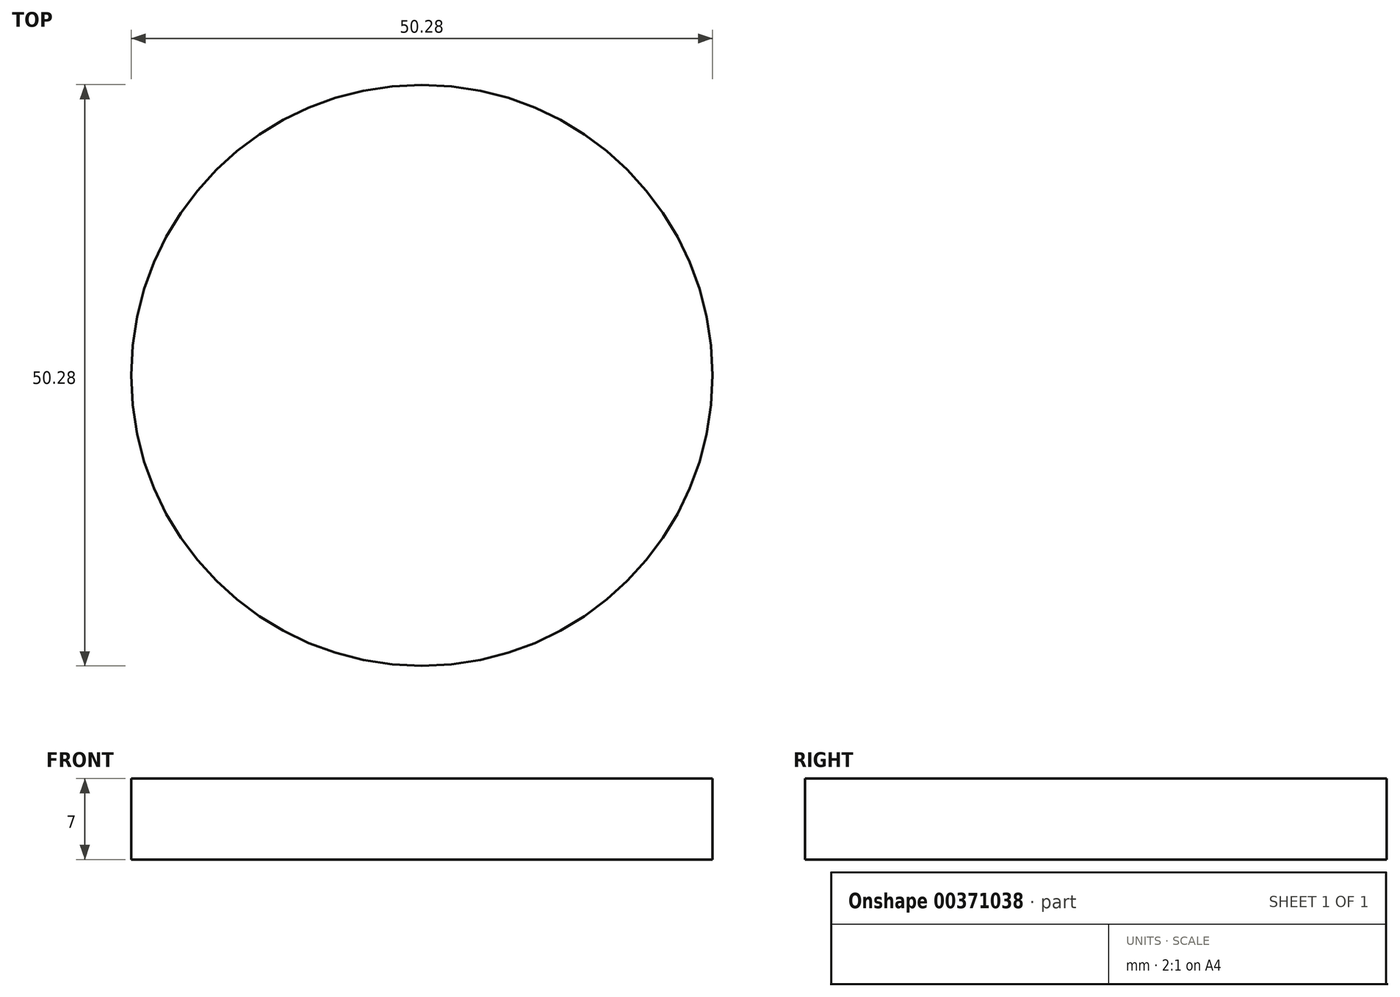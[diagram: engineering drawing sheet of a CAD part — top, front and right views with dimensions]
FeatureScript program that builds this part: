
annotation { "Feature Type Name" : "Feature", "Feature Type Description" : "" }
export const myFeature = defineFeature(function(context is Context, id is Id, definition is map)
    precondition{}
    {
        {
            var Q0;
            Q0=qCreatedBy(makeId("Top.planeOp"),FACE);
            var sketch = newSketch(context, id + "F0", { "sketchPlane" : qUnion([Q0])});
            skCircle(sketch, "E0", {"center": v(0, 0) * mm, "radius": 25.14 * mm});
            skSolve(sketch);
        }
        {
            var Q0;
            Q0 = qSketchRegion(id + "F0", true);
            extrude(context, id + "F1", {"entities" : qUnion([Q0]), "depth" : 7 * mm});
        }
    });
